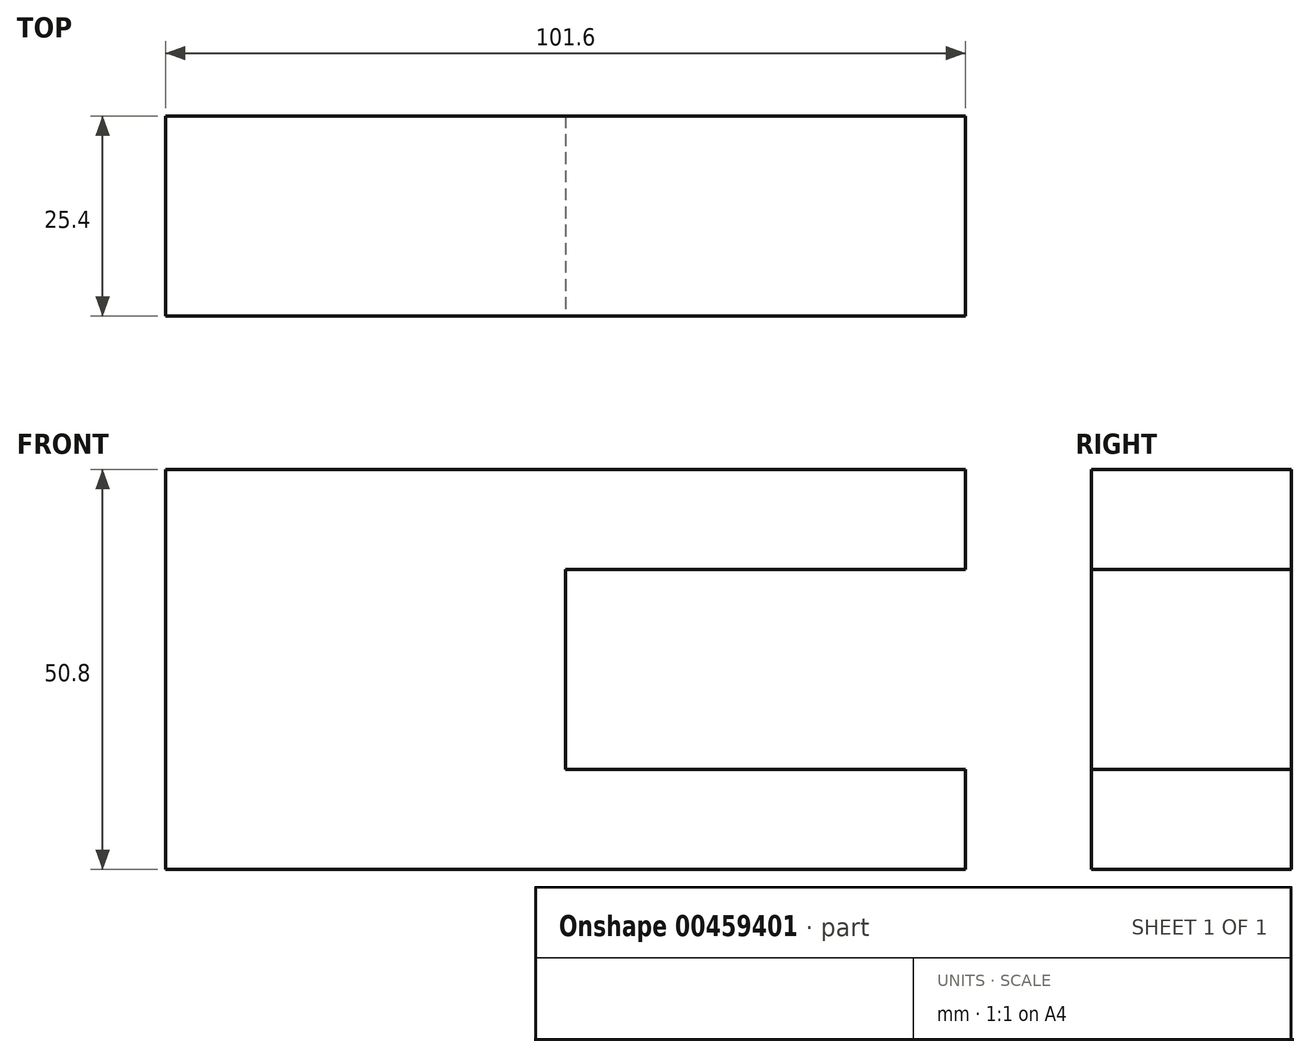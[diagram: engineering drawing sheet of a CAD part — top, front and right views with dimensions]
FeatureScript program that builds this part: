
annotation { "Feature Type Name" : "Feature", "Feature Type Description" : "" }
export const myFeature = defineFeature(function(context is Context, id is Id, definition is map)
    precondition{}
    {
        {
            var Q0;
            Q0=qCreatedBy(makeId("Front.planeOp"),FACE);
            var sketch = newSketch(context, id + "F0", { "sketchPlane" : qUnion([Q0])});
            skLineSegment(sketch, "E0.bottom", {"start": v(-50.8, -25.4) * mm, "end": v(50.8, -25.4) * mm});
            skLineSegment(sketch, "E0.top", {"start": v(-50.8, 25.4) * mm, "end": v(50.8, 25.4) * mm});
            skLineSegment(sketch, "E0.left", {"start": v(-50.8, -25.4) * mm, "end": v(-50.8, 25.4) * mm});
            skLineSegment(sketch, "E0.right", {"start": v(50.8, -25.4) * mm, "end": v(50.8, 25.4) * mm});
            skPoint(sketch, "E0.middle", {"position": v(0, 0) * mm});
            skSolve(sketch);
        }
        {
            var Q0;
            Q0 = qSketchRegion(id + "F0", true);
            extrude(context, id + "F1", {"entities" : qUnion([Q0]), "depth" : 25.4 * mm});
        }
        {
            var Q0;
            Q0=makeQuery(id+"F1.opExtrude","CAP_FACE",FACE,{"disambiguationData":[OSD([sQuery(id+"F0.wireOp",EDGE,"E0.bottom"),sQuery(id+"F0.wireOp",EDGE,"E0.top"),sQuery(id+"F0.wireOp",EDGE,"E0.left"),sQuery(id+"F0.wireOp",EDGE,"E0.right")])],"isStart":false});
            var sketch = newSketch(context, id + "F2", { "sketchPlane" : qUnion([Q0])});
            skLineSegment(sketch, "E1.bottom", {"start": v(50.8, 12.7) * mm, "end": v(0, 12.7) * mm});
            skLineSegment(sketch, "E1.top", {"start": v(50.8, -12.7) * mm, "end": v(0, -12.7) * mm});
            skLineSegment(sketch, "E1.left", {"start": v(50.8, 12.7) * mm, "end": v(50.8, -12.7) * mm});
            skLineSegment(sketch, "E1.right", {"start": v(0, 12.7) * mm, "end": v(0, -12.7) * mm});
            skSolve(sketch);
        }
        {
            var Q0;
            Q0=makeQuery(id+"F2.imprint","IMPRINT",FACE,{"disambiguationData":[TD([[makeQuery(id+"F2.imprint","IMPRINT",EDGE,{"derivedFrom":sQuery(id+"F2.wireOp",EDGE,"E1.bottom")}),1.0]])]});
            extrude(context, id + "F3", {"entities" : qUnion([Q0]), "operationType" : NewBodyOperationType.REMOVE, "endBound" : BoundingType.THROUGH_ALL, "oppositeDirection" : true, "depth" : 25.4 * mm});
        }
    });
